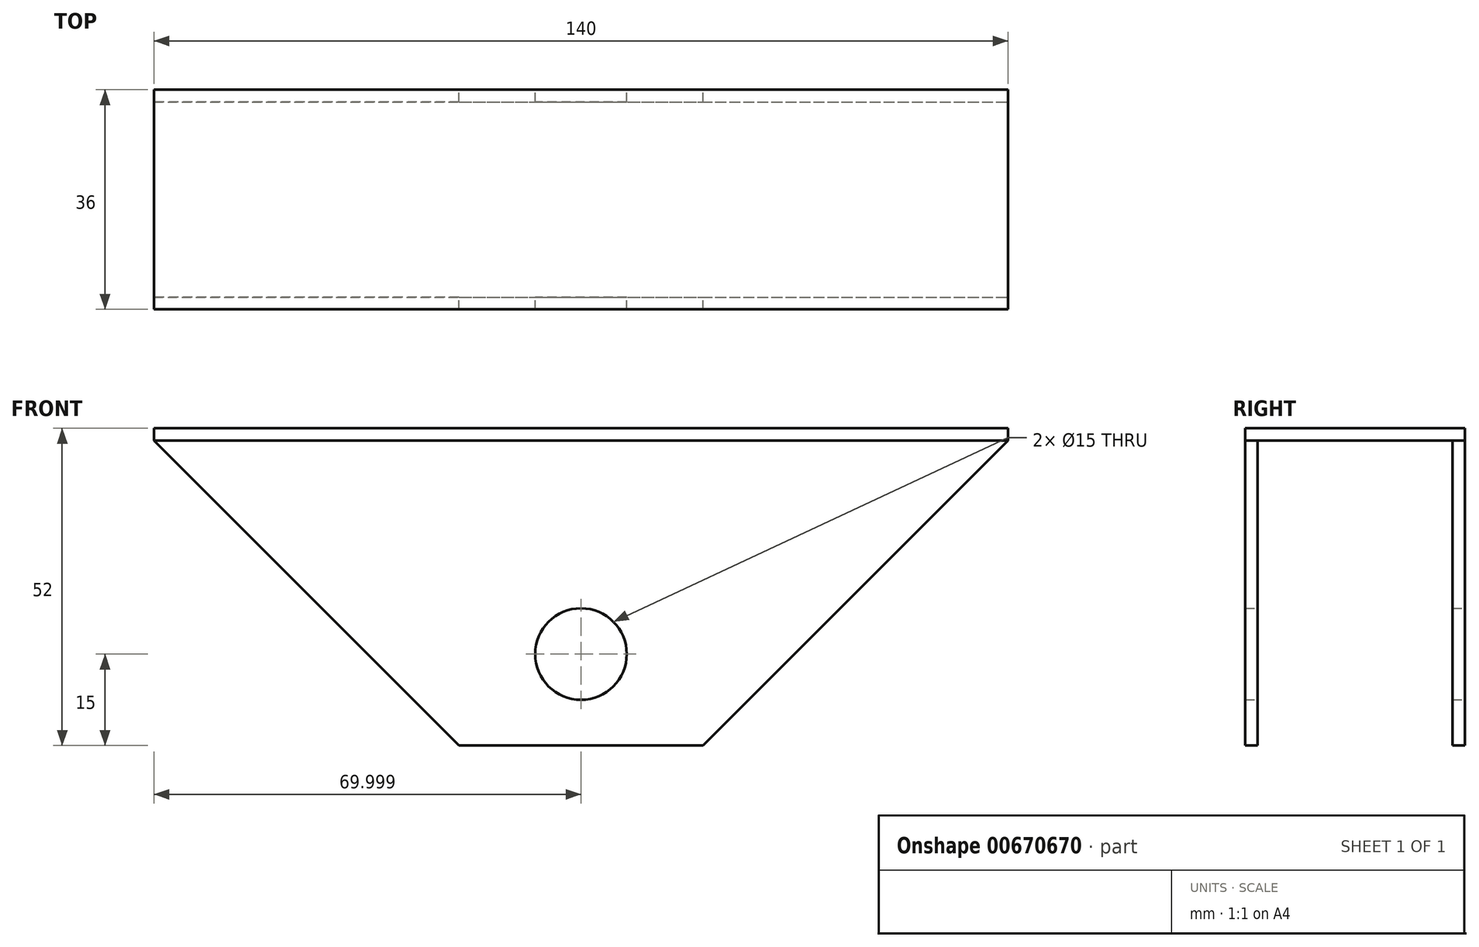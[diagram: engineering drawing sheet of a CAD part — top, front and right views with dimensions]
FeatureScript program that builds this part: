
annotation { "Feature Type Name" : "Feature", "Feature Type Description" : "" }
export const myFeature = defineFeature(function(context is Context, id is Id, definition is map)
    precondition{}
    {
        {
            var Q0;
            Q0=qCreatedBy(makeId("Front.planeOp"),FACE);
            var sketch = newSketch(context, id + "F0", { "sketchPlane" : qUnion([Q0])});
            skLineSegment(sketch, "E0.bottom", {"start": v(-67.52, 35.1) * mm, "end": v(72.48, 35.1) * mm});
            skLineSegment(sketch, "E0.top", {"start": v(-67.52, 33.1) * mm, "end": v(72.48, 33.1) * mm});
            skLineSegment(sketch, "E0.left", {"start": v(-67.52, 35.1) * mm, "end": v(-67.52, 33.1) * mm});
            skLineSegment(sketch, "E0.right", {"start": v(72.48, 35.1) * mm, "end": v(72.48, 33.1) * mm});
            skCircle(sketch, "E1", {"center": v(2.48, -1.9) * mm, "radius": 7.5 * mm});
            skLineSegment(sketch, "E2", {"start": v(-17.52, -16.9) * mm, "end": v(-67.52, 33.1) * mm});
            skLineSegment(sketch, "E3", {"start": v(-17.52, -16.9) * mm, "end": v(22.48, -16.9) * mm});
            skLineSegment(sketch, "E4", {"start": v(22.48, -16.9) * mm, "end": v(72.48, 33.1) * mm});
            skSolve(sketch);
        }
        {
            var Q0;
            Q0=makeQuery(id+"F0.imprint","IMPRINT",FACE,{"disambiguationData":[TD([[makeQuery(id+"F0.imprint","IMPRINT",EDGE,{"derivedFrom":sQuery(id+"F0.wireOp",EDGE,"E0.top")}),-1.0]])]});
            extrude(context, id + "F1", {"entities" : qUnion([Q0]), "depth" : 2 * mm, "offsetDistance" : 25 * mm});
        }
        {
            var Q0;
            Q0=makeQuery(id+"F0.imprint","IMPRINT",FACE,{"disambiguationData":[TD([[makeQuery(id+"F0.imprint","IMPRINT",EDGE,{"derivedFrom":sQuery(id+"F0.wireOp",EDGE,"E0.bottom")}),-1.0]])]});
            extrude(context, id + "F2", {"entities" : qUnion([Q0]), "operationType" : NewBodyOperationType.ADD, "depth" : 36 * mm, "offsetDistance" : 25 * mm});
        }
        {
            var Q0;
            Q0=makeQuery(id+"F0.imprint","IMPRINT",FACE,{"disambiguationData":[TD([[makeQuery(id+"F0.imprint","IMPRINT",EDGE,{"derivedFrom":sQuery(id+"F0.wireOp",EDGE,"E0.top")}),-1.0]])]});
            extrude(context, id + "F3", {"entities" : qUnion([Q0]), "depth" : 2 * mm, "offsetDistance" : 25 * mm});
        }
        {
            var Q0;
            Q0=makeQuery(id+"F3.opExtrude","SWEPT_BODY",BODY,{"disambiguationData":[OSD([sQuery(id+"F0.wireOp",EDGE,"E0.top"),sQuery(id+"F0.wireOp",EDGE,"E1"),sQuery(id+"F0.wireOp",EDGE,"E2"),sQuery(id+"F0.wireOp",EDGE,"E3"),sQuery(id+"F0.wireOp",EDGE,"E4")])]});
            transform(context, id + "F4", {"entities" : qUnion([Q0]), "transformType" : TransformType.TRANSLATION_3D, "dx" : 0 * mm, "dy" : -34 * mm, "dz" : 0 * mm, "makeCopy" : false});
        }
    });
